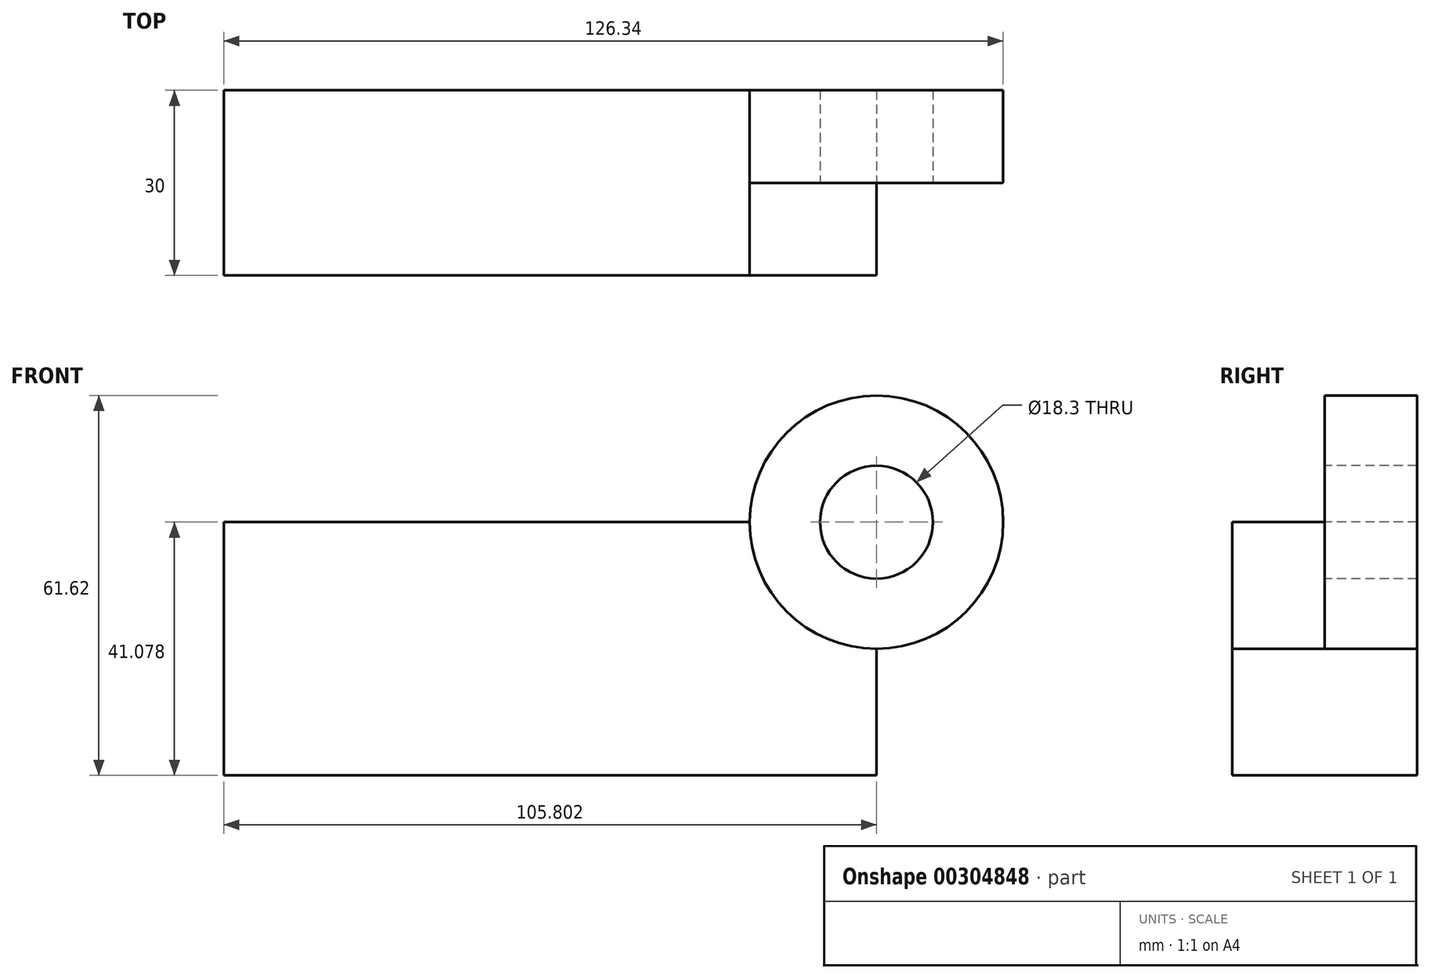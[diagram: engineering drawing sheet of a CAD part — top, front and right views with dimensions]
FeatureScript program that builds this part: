
annotation { "Feature Type Name" : "Feature", "Feature Type Description" : "" }
export const myFeature = defineFeature(function(context is Context, id is Id, definition is map)
    precondition{}
    {
        {
            var Q0;
            Q0=qCreatedBy(makeId("Front.planeOp"),FACE);
            var sketch = newSketch(context, id + "F0", { "sketchPlane" : qUnion([Q0])});
            skLineSegment(sketch, "E0.bottom", {"start": v(-52.9, -20.54) * mm, "end": v(52.9, -20.54) * mm});
            skLineSegment(sketch, "E0.top", {"start": v(-52.9, 20.54) * mm, "end": v(52.9, 20.54) * mm});
            skLineSegment(sketch, "E0.left", {"start": v(-52.9, -20.54) * mm, "end": v(-52.9, 20.54) * mm});
            skLineSegment(sketch, "E0.right", {"start": v(52.9, -20.54) * mm, "end": v(52.9, 20.54) * mm});
            skPoint(sketch, "E0.middle", {"position": v(0, 0) * mm});
            skPoint(sketch, "E1", {"position": v(52.9, 0) * mm});
            skCircle(sketch, "E2", {"center": v(52.9, 20.54) * mm, "radius": 20.54 * mm});
            skCircle(sketch, "E3", {"center": v(52.9, 20.54) * mm, "radius": 9.15 * mm});
            skSolve(sketch);
        }
        {
            var Q0;
            {var subQ5=sQuery(id+"F0.wireOp",EDGE,"E0.bottom");Q0=makeQuery(id+"F0.imprint","IMPRINT",FACE,{"disambiguationData":[TD([[makeQuery(id+"F0.imprint","IMPRINT",EDGE,{"derivedFrom":subQ5}),1.0]])]});}
            extrude(context, id + "F1", {"entities" : qUnion([Q0]), "oppositeDirection" : true, "depth" : 15 * mm});
        }
        {
            var Q0;
            Q0=makeQuery(id+"F1.opExtrude","CAP_FACE",FACE,{"disambiguationData":[OSD([sQuery(id+"F0.wireOp",EDGE,"E0.bottom"),sQuery(id+"F0.wireOp",EDGE,"E0.top"),sQuery(id+"F0.wireOp",EDGE,"E0.left"),sQuery(id+"F0.wireOp",EDGE,"E0.right"),sQuery(id+"F0.wireOp",EDGE,"E2")])],"isStart":true});
            extrude(context, id + "F2", {"entities" : qUnion([Q0]), "operationType" : NewBodyOperationType.ADD, "depth" : 15 * mm});
        }
        {
            var Q0;
            {var subQ0=sQuery(id+"F0.wireOp",EDGE,"E2");var subQ1=sQuery(id+"F0.wireOp",EDGE,"E0.top");var subQ2=makeQuery(id+"F0.imprint","INTERSECT",VERTEX,{"derivedFrom":[subQ1,subQ0]});Q0=makeQuery(id+"F0.imprint","IMPRINT",FACE,{"disambiguationData":[TD([[makeQuery(id+"F0.imprint","IMPRINT",EDGE,{"disambiguationData":[TD([[subQ2,-1.0]])],"derivedFrom":subQ1}),1.0]])]});}
            var Q1;
            {var subQ0=sQuery(id+"F0.wireOp",EDGE,"E2");var subQ1=sQuery(id+"F0.wireOp",EDGE,"E0.top");var subQ2=makeQuery(id+"F0.imprint","INTERSECT",VERTEX,{"derivedFrom":[subQ1,subQ0]});Q1=makeQuery(id+"F0.imprint","IMPRINT",FACE,{"disambiguationData":[TD([[makeQuery(id+"F0.imprint","IMPRINT",EDGE,{"disambiguationData":[TD([[subQ2,-1.0]])],"derivedFrom":subQ1}),-1.0]])]});}
            extrude(context, id + "F3", {"entities" : qUnion([Q0, Q1]), "operationType" : NewBodyOperationType.ADD, "oppositeDirection" : true, "depth" : 15 * mm});
        }
    });
